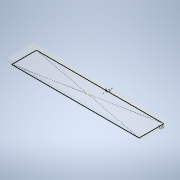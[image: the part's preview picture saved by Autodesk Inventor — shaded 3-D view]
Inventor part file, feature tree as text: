
AUTODESK INVENTOR PART (.ipt)
format: ipt  version: 2020.1 (Build 241239000, 239)  size: 112,128 bytes
history: native  units: mm
features: extrude x2, sketch x2
ambient origin geometry x8: Origin, YZ Plane, XZ Plane, XY Plane, X Axis, Y Axis, Z Axis, Center Point
bodies: Solid1 (feature_tree)
feature tree (4):
  extrude  "Extrusion1"  Depth=12.0mm
  extrude  "Extrusion2"  Depth=0.5mm
  sketch  "Sketch1"  dims[d0=60.0mm d1=12.0mm]
  sketch  "Sketch2"  dims[d2=2.0mm d3=0.0mm d4=0.5mm d5=1.6mm d6=0.02mm d7=0.0mm]
